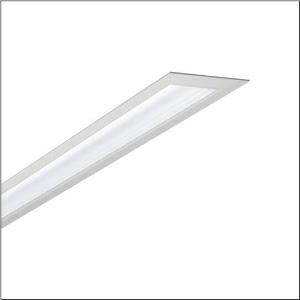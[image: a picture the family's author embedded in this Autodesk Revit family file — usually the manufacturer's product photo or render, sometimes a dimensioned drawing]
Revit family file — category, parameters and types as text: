
# Revit family: silica_r_5mx11bd2w4a_6c5b
name_source: partatom
category: Lighting Fixtures
units: mm (PartAtom-declared; Revit-internal decimal feet)

## family parameters
Cut with Voids When Loaded = No
Host = Face
Light Source = No
Part Type = Normal
Room Calculation Point = No
Round Connector Dimension = Use Diameter
Shared = No

## types (1)
- --- (1 x LED, 9910 lm, 60.1 W, 4000K)
    Apparent Load = 60 VA
    CIE Flux Codes = 82 97 100 100 100
    Color Rendering = 80
    Color Temperature = 4000K
    Default Elevation = 1800 mm
    Description = Silica®, office luminaire, of aluminium, light emission: direct distribution, primary light characteristic: symmetric, installation type: recessed, LED, rated luminous flux: 9.910lm, luminous efficacy: 165lm/W, light colour: 840, colour temperature: 4000K, control gear: ECG DALI, with terminal, 3+2-pole, max. 2.5mm², mains connection: 230V, AC, 50/60Hz, rated input power: 60W, luminaire housing, of aluminium, matt pure white (RAL 9010), length: 2.864mm, width: 93mm, height: 60mm, end cap, of diecast zinc, pure white (RAL 9010), protection rating (complete): IP20, insulation class (complete): insulation class I (protective earthing), certification: CE, permissible operating ambient temperature: 0..+35°C, standard: EN 50419, packaging unit: 1 piece
    Height = 0 mm  [stored 0 ft]
    Lamp = 1 x LED
    Lamp Light Flux = 9910 lm
    Lamp Power = 60.1 W
    Lamp count = 1
    Length = 2865 mm
    Luminous efficacy = 165 lm/W
    Manufacturer = Siteco
    ModVariant = No
    Model = 5MX11BD2W4A
    Mounting Place = Ceiling
    Mounting Type = Recessed
    Number of Poles = 1
    OnlyDefault = Yes
    Power Factor = 1
    Product Name = Silica®
    Product group = office luminaire | ceiling recessed
    ProductGroupID = 401
    Protection Class = Protection class I
    Protection Degree = IP 20
    RLX_Detail_Level = 1
    RLX_Emergency_Light_Flux = 0 lm
    RLX_Emergency_Type = 0
    RLX_Emergency_Type_DB = No
    RlxData = <blob elided: 24337 chars, md5=d53c247a>
    Socket = socket
    Standby Power = 0 W
    System Light Flux = 9910 lm
    System Power = 60 W
    Type Comments = factory setting: luminous flux: 100 % | dim-lin: 254 | 336 mA
    Type Image = l_1004825.jpg
    URL = http://relux.com
    VarID = @adj_155340
    Voltage = 0 V
    Weight = 0.00 kg
    Width = 93 mm

note: [stored X ft] marks values corroborated as IEEE doubles in the binary element streams (Revit-internal decimal feet)

## geometry (parser evidence)
native form markers: Blend x4, Sweep x11
no freeform markers — native parametric forms only
